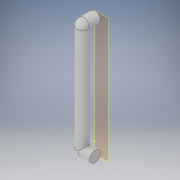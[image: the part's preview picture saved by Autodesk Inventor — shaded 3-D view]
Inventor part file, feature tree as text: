
AUTODESK INVENTOR PART (.ipt)
format: ipt  version: 2019 (Build 230136000, 136)  size: 117,760 bytes
history: native  units: mm
features: sketch x6, plane x2, sweep x1
ambient origin geometry x8: Origin, YZ Plane, XZ Plane, XY Plane, X Axis, Y Axis, Z Axis, Center Point
bodies: Solid1 (feature_tree)
feature tree (9):
  sketch  "Sketch1"  dims[d0=500.0mm d1=60.0mm]
  sketch  "3D Sketch1"
  sketch  "Sketch2"  dims[d2=60.0mm]
  sketch  "Sketch3"  dims[d5=60.0mm]
  plane  "Work Plane1"
  sketch  "Sketch4"  dims[d6=50.0mm]
  plane  "Work Plane2"
  sketch  "Sketch5"  dims[d7=-60.0mm d8=7.0mm d9=7.0mm d10=0.0mm d11=0.0mm]
  sweep  "Sweep1"
